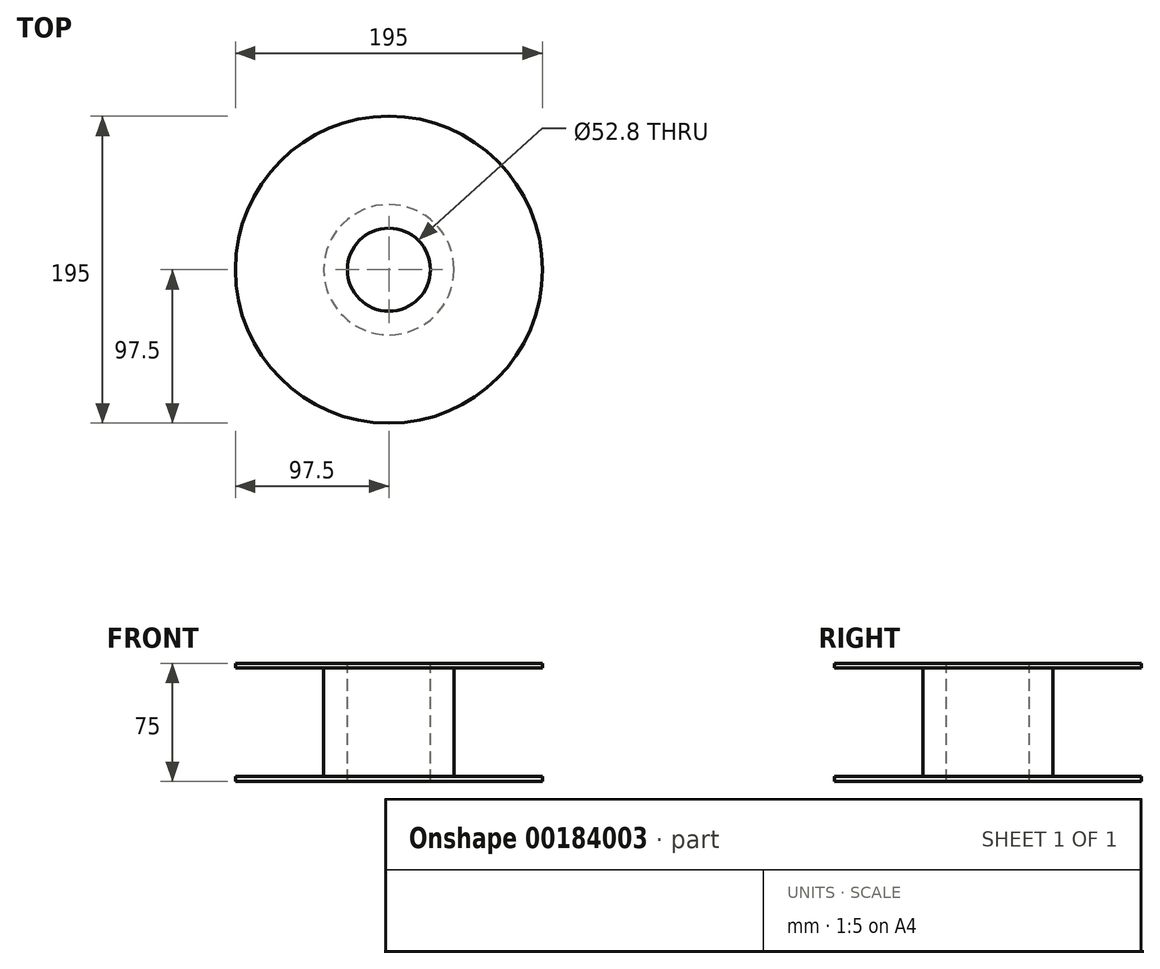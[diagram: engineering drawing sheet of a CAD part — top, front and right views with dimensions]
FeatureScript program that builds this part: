
annotation { "Feature Type Name" : "Feature", "Feature Type Description" : "" }
export const myFeature = defineFeature(function(context is Context, id is Id, definition is map)
    precondition{}
    {
        {
            var Q0;
            Q0=qCreatedBy(makeId("Front.planeOp"),FACE);
            var sketch = newSketch(context, id + "F0", { "sketchPlane" : qUnion([Q0])});
            skLineSegment(sketch, "E0", {"start": v(0, 37.5) * mm, "end": v(0, -37.5) * mm, "construction": true});
            skLineSegment(sketch, "E1", {"start": v(0, 37.5) * mm, "end": v(-97.5, 37.5) * mm});
            skLineSegment(sketch, "E2", {"start": v(-97.5, 37.5) * mm, "end": v(-97.5, 34.5) * mm});
            skLineSegment(sketch, "E3", {"start": v(-97.5, 34.5) * mm, "end": v(-41.4, 34.5) * mm});
            skLineSegment(sketch, "E4", {"start": v(-41.4, 34.5) * mm, "end": v(-41.4, -34.5) * mm});
            skLineSegment(sketch, "E5", {"start": v(-41.4, -34.5) * mm, "end": v(-97.5, -34.5) * mm});
            skLineSegment(sketch, "E6", {"start": v(-97.5, -34.5) * mm, "end": v(-97.5, -37.5) * mm});
            skLineSegment(sketch, "E7", {"start": v(-97.5, -37.5) * mm, "end": v(0, -37.5) * mm});
            skLineSegment(sketch, "E8", {"start": v(-26.4, 37.5) * mm, "end": v(-26.4, -37.5) * mm});
            skSolve(sketch);
        }
        {
            var Q0;
            Q0=qSketchRegion(id+"F0",true);
            var Q1;
            Q1=sQuery(id+"F0.wireOp",EDGE,"E0");
            revolve(context, id + "F1", {"entities" : qUnion([Q0]), "axis" : qUnion([Q1]), "revolveType" : RevolveType.FULL});
        }
    });
